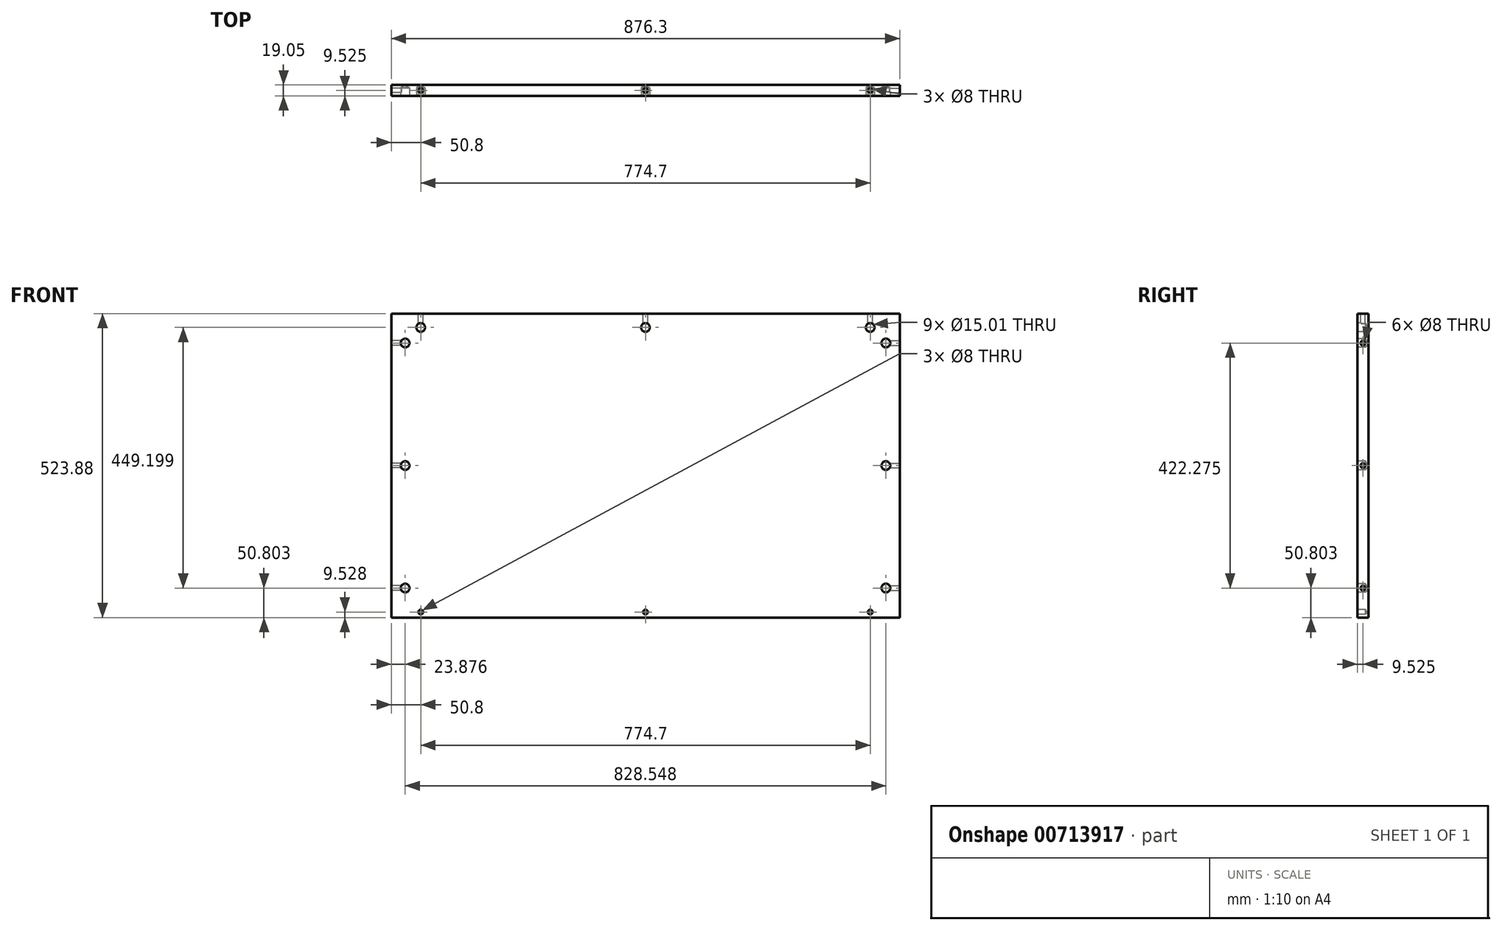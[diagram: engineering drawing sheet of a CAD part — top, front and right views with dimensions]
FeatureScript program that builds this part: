
annotation { "Feature Type Name" : "Feature", "Feature Type Description" : "" }
export const myFeature = defineFeature(function(context is Context, id is Id, definition is map)
    precondition{}
    {
        {
            var Q0;
            Q0=qCreatedBy(makeId("Front.planeOp"),FACE);
            var sketch = newSketch(context, id + "F0", { "sketchPlane" : qUnion([Q0])});
            skLineSegment(sketch, "E0.bottom", {"start": v(438.15, 261.94) * mm, "end": v(-438.15, 261.94) * mm});
            skLineSegment(sketch, "E0.top", {"start": v(438.15, -261.94) * mm, "end": v(-438.15, -261.94) * mm});
            skLineSegment(sketch, "E0.left", {"start": v(438.15, 261.94) * mm, "end": v(438.15, -261.94) * mm});
            skLineSegment(sketch, "E0.right", {"start": v(-438.15, 261.94) * mm, "end": v(-438.15, -261.94) * mm});
            skPoint(sketch, "E0.middle", {"position": v(0, 0) * mm});
            skSolve(sketch);
        }
        {
            var Q0;
            Q0=makeQuery(id+"F0.imprint","IMPRINT",FACE,{"disambiguationData":[TD([[makeQuery(id+"F0.imprint","IMPRINT",EDGE,{"derivedFrom":sQuery(id+"F0.wireOp",EDGE,"E0.bottom")}),1.0]])]});
            extrude(context, id + "F1", {"entities" : qUnion([Q0]), "depth" : 19.05 * mm, "offsetDistance" : 25.4 * mm});
        }
        {
            var Q0;
            Q0=makeQuery(id+"F1.opExtrude","CAP_FACE",FACE,{"disambiguationData":[OSD([sQuery(id+"F0.wireOp",EDGE,"E0.bottom"),sQuery(id+"F0.wireOp",EDGE,"E0.top"),sQuery(id+"F0.wireOp",EDGE,"E0.left"),sQuery(id+"F0.wireOp",EDGE,"E0.right")])],"isStart":false});
            var sketch = newSketch(context, id + "F2", { "sketchPlane" : qUnion([Q0])});
            skLineSegment(sketch, "E1", {"start": v(-438.15, 261.94) * mm, "end": v(-414.27, 261.94) * mm});
            skLineSegment(sketch, "E2", {"start": v(-414.27, 261.94) * mm, "end": v(-414.27, -261.94) * mm});
            skLineSegment(sketch, "E3", {"start": v(438.15, 261.94) * mm, "end": v(414.27, 261.94) * mm});
            skLineSegment(sketch, "E4", {"start": v(414.27, 261.94) * mm, "end": v(414.27, -261.94) * mm});
            skLineSegment(sketch, "E5", {"start": v(-438.15, -261.94) * mm, "end": v(-438.15, -252.41) * mm});
            skLineSegment(sketch, "E6", {"start": v(-438.15, -252.41) * mm, "end": v(438.15, -252.41) * mm});
            skLineSegment(sketch, "E7", {"start": v(-438.15, 261.94) * mm, "end": v(-438.15, 238.06) * mm});
            skLineSegment(sketch, "E8", {"start": v(-438.15, 238.06) * mm, "end": v(438.15, 238.06) * mm});
            skLineSegment(sketch, "E9", {"start": v(0, 238.06) * mm, "end": v(0, 261.94) * mm});
            skLineSegment(sketch, "E10", {"start": v(-414.27, 0) * mm, "end": v(-438.15, 0) * mm});
            skLineSegment(sketch, "E11", {"start": v(414.27, 0) * mm, "end": v(438.15, 0) * mm});
            skLineSegment(sketch, "E12", {"start": v(0, -261.94) * mm, "end": v(0, -252.41) * mm});
            skLineSegment(sketch, "E13", {"start": v(-438.15, -252.41) * mm, "end": v(-387.35, -252.41) * mm});
            skLineSegment(sketch, "E14", {"start": v(438.15, -252.41) * mm, "end": v(387.35, -252.41) * mm});
            skLineSegment(sketch, "E15", {"start": v(-414.27, 261.94) * mm, "end": v(-414.27, 211.14) * mm});
            skLineSegment(sketch, "E16", {"start": v(-414.27, -261.94) * mm, "end": v(-414.27, -211.14) * mm});
            skLineSegment(sketch, "E17", {"start": v(414.27, -261.94) * mm, "end": v(414.27, -211.14) * mm});
            skLineSegment(sketch, "E18", {"start": v(414.27, 261.94) * mm, "end": v(414.27, 211.14) * mm});
            skLineSegment(sketch, "E19", {"start": v(-438.15, 238.06) * mm, "end": v(-387.35, 238.06) * mm});
            skLineSegment(sketch, "E20", {"start": v(438.15, 238.06) * mm, "end": v(387.35, 238.06) * mm});
            skPoint(sketch, "E21", {"position": v(-387.35, 238.06) * mm});
            skPoint(sketch, "E22", {"position": v(-414.27, 211.14) * mm});
            skPoint(sketch, "E23", {"position": v(0, 238.06) * mm});
            skPoint(sketch, "E24", {"position": v(387.35, 238.06) * mm});
            skPoint(sketch, "E25", {"position": v(414.27, 211.14) * mm});
            skPoint(sketch, "E26", {"position": v(414.27, 0) * mm});
            skPoint(sketch, "E27", {"position": v(-414.27, 0) * mm});
            skPoint(sketch, "E28", {"position": v(414.27, -211.14) * mm});
            skPoint(sketch, "E29", {"position": v(387.35, -252.41) * mm});
            skPoint(sketch, "E30", {"position": v(0, -252.41) * mm});
            skPoint(sketch, "E31", {"position": v(-387.35, -252.41) * mm});
            skPoint(sketch, "E32", {"position": v(-414.27, -211.14) * mm});
            skSolve(sketch);
        }
        {
            var Q0;
            Q0=sQuery(id+"F2.wireOp",VERTEX,"E21");
            var Q1;
            Q1=sQuery(id+"F2.wireOp",VERTEX,"E22");
            var Q2;
            Q2=sQuery(id+"F2.wireOp",VERTEX,"E27");
            var Q3;
            Q3=sQuery(id+"F2.wireOp",VERTEX,"E32");
            var Q4;
            Q4=sQuery(id+"F2.wireOp",VERTEX,"E23");
            var Q5;
            Q5=sQuery(id+"F2.wireOp",VERTEX,"E24");
            var Q6;
            Q6=sQuery(id+"F2.wireOp",VERTEX,"E25");
            var Q7;
            Q7=sQuery(id+"F2.wireOp",VERTEX,"E26");
            var Q8;
            Q8=sQuery(id+"F2.wireOp",VERTEX,"E28");
            var Q9;
            Q9=makeQuery(id+"F1.opExtrude","SWEPT_BODY",BODY,{"disambiguationData":[OSD([sQuery(id+"F0.wireOp",EDGE,"E0.bottom"),sQuery(id+"F0.wireOp",EDGE,"E0.top"),sQuery(id+"F0.wireOp",EDGE,"E0.left"),sQuery(id+"F0.wireOp",EDGE,"E0.right")])]});
            hole(context, id + "F3", {"style" : HoleStyle.SIMPLE, "endStyle" : HoleEndStyle.BLIND, "holeDiameter" : 15 * mm, "majorDiameter" : 6.35 * mm, "holeDepth" : 14.22 * mm, "isTappedThrough" : true, "tappedDepth" : 12.7 * mm, "tapClearance" : 3, "startFromSketch" : true, "locations" : qUnion([Q0, Q1, Q2, Q3, Q4, Q5, Q6, Q7, Q8]), "scope" : qUnion([Q9])});
        }
        {
            var Q0;
            Q0=sQuery(id+"F2.wireOp",VERTEX,"E31");
            var Q1;
            Q1=sQuery(id+"F2.wireOp",VERTEX,"E30");
            var Q2;
            Q2=sQuery(id+"F2.wireOp",VERTEX,"E29");
            var Q3;
            Q3=makeQuery(id+"F1.opExtrude","SWEPT_BODY",BODY,{"disambiguationData":[OSD([sQuery(id+"F0.wireOp",EDGE,"E0.bottom"),sQuery(id+"F0.wireOp",EDGE,"E0.top"),sQuery(id+"F0.wireOp",EDGE,"E0.left"),sQuery(id+"F0.wireOp",EDGE,"E0.right")])]});
            hole(context, id + "F4", {"style" : HoleStyle.SIMPLE, "endStyle" : HoleEndStyle.BLIND, "holeDiameter" : 8 * mm, "majorDiameter" : 6.35 * mm, "holeDepth" : 14.22 * mm, "isTappedThrough" : true, "tappedDepth" : 12.7 * mm, "tapClearance" : 3, "startFromSketch" : true, "locations" : qUnion([Q0, Q1, Q2]), "scope" : qUnion([Q3])});
        }
        {
            var Q0;
            Q0=makeQuery(id+"F1.opExtrude","SWEPT_FACE",FACE,{"disambiguationData":[OSD([sQuery(id+"F0.wireOp",EDGE,"E0.left")])]});
            var sketch = newSketch(context, id + "F5", { "sketchPlane" : qUnion([Q0])});
            skLineSegment(sketch, "E33", {"start": v(-9.53, 261.94) * mm, "end": v(-9.53, 211.14) * mm});
            skLineSegment(sketch, "E34", {"start": v(-9.53, -261.94) * mm, "end": v(-9.53, -211.14) * mm});
            skLineSegment(sketch, "E35", {"start": v(-19.05, 0) * mm, "end": v(-9.53, 0) * mm});
            skPoint(sketch, "E36", {"position": v(-9.53, 211.14) * mm});
            skPoint(sketch, "E37", {"position": v(-9.53, 0) * mm});
            skPoint(sketch, "E38", {"position": v(-9.53, -211.14) * mm});
            skSolve(sketch);
        }
        {
            var Q0;
            Q0=sQuery(id+"F5.wireOp",VERTEX,"E36");
            var Q1;
            Q1=sQuery(id+"F5.wireOp",VERTEX,"E37");
            var Q2;
            Q2=sQuery(id+"F5.wireOp",VERTEX,"E38");
            var Q3;
            Q3=makeQuery(id+"F1.opExtrude","SWEPT_BODY",BODY,{"disambiguationData":[OSD([sQuery(id+"F0.wireOp",EDGE,"E0.bottom"),sQuery(id+"F0.wireOp",EDGE,"E0.top"),sQuery(id+"F0.wireOp",EDGE,"E0.left"),sQuery(id+"F0.wireOp",EDGE,"E0.right")])]});
            hole(context, id + "F6", {"style" : HoleStyle.SIMPLE, "endStyle" : HoleEndStyle.BLIND, "holeDiameter" : 8 * mm, "majorDiameter" : 6.35 * mm, "holeDepth" : 25.4 * mm, "isTappedThrough" : true, "tappedDepth" : 12.7 * mm, "tapClearance" : 3, "startFromSketch" : true, "locations" : qUnion([Q0, Q1, Q2]), "scope" : qUnion([Q3])});
        }
        {
            var Q0;
            Q0=makeQuery(id+"F1.opExtrude","SWEPT_FACE",FACE,{"disambiguationData":[OSD([sQuery(id+"F0.wireOp",EDGE,"E0.right")])]});
            var sketch = newSketch(context, id + "F7", { "sketchPlane" : qUnion([Q0])});
            skLineSegment(sketch, "E39", {"start": v(9.53, 261.94) * mm, "end": v(9.53, 211.14) * mm});
            skLineSegment(sketch, "E40", {"start": v(19.05, 0) * mm, "end": v(9.53, 0) * mm});
            skLineSegment(sketch, "E41", {"start": v(9.53, -261.94) * mm, "end": v(9.53, -211.14) * mm});
            skSolve(sketch);
        }
        {
            var Q0;
            Q0=sQuery(id+"F7.wireOp",VERTEX,"E39.end");
            var Q1;
            Q1=sQuery(id+"F7.wireOp",VERTEX,"E40.end");
            var Q2;
            Q2=sQuery(id+"F7.wireOp",VERTEX,"E41.end");
            var Q3;
            Q3=makeQuery(id+"F1.opExtrude","SWEPT_BODY",BODY,{"disambiguationData":[OSD([sQuery(id+"F0.wireOp",EDGE,"E0.bottom"),sQuery(id+"F0.wireOp",EDGE,"E0.top"),sQuery(id+"F0.wireOp",EDGE,"E0.left"),sQuery(id+"F0.wireOp",EDGE,"E0.right")])]});
            hole(context, id + "F8", {"style" : HoleStyle.SIMPLE, "endStyle" : HoleEndStyle.BLIND, "holeDiameter" : 8 * mm, "majorDiameter" : 6.35 * mm, "holeDepth" : 25.4 * mm, "isTappedThrough" : true, "tappedDepth" : 12.7 * mm, "tapClearance" : 3, "startFromSketch" : true, "locations" : qUnion([Q0, Q1, Q2]), "scope" : qUnion([Q3])});
        }
        {
            var Q0;
            Q0=makeQuery(id+"F1.opExtrude","SWEPT_FACE",FACE,{"disambiguationData":[OSD([sQuery(id+"F0.wireOp",EDGE,"E0.bottom")])]});
            var sketch = newSketch(context, id + "F9", { "sketchPlane" : qUnion([Q0])});
            skLineSegment(sketch, "E42", {"start": v(-438.15, -9.53) * mm, "end": v(-387.35, -9.53) * mm});
            skLineSegment(sketch, "E43", {"start": v(0, -19.05) * mm, "end": v(0, -9.53) * mm});
            skLineSegment(sketch, "E44", {"start": v(438.15, -9.53) * mm, "end": v(387.35, -9.53) * mm});
            skPoint(sketch, "E45", {"position": v(-387.35, -9.53) * mm});
            skPoint(sketch, "E46", {"position": v(0, -9.53) * mm});
            skPoint(sketch, "E47", {"position": v(387.35, -9.53) * mm});
            skSolve(sketch);
        }
        {
            var Q0;
            Q0=sQuery(id+"F9.wireOp",VERTEX,"E45");
            var Q1;
            Q1=sQuery(id+"F9.wireOp",VERTEX,"E46");
            var Q2;
            Q2=sQuery(id+"F9.wireOp",VERTEX,"E47");
            var Q3;
            Q3=makeQuery(id+"F1.opExtrude","SWEPT_BODY",BODY,{"disambiguationData":[OSD([sQuery(id+"F0.wireOp",EDGE,"E0.bottom"),sQuery(id+"F0.wireOp",EDGE,"E0.top"),sQuery(id+"F0.wireOp",EDGE,"E0.left"),sQuery(id+"F0.wireOp",EDGE,"E0.right")])]});
            hole(context, id + "F10", {"style" : HoleStyle.SIMPLE, "endStyle" : HoleEndStyle.BLIND, "holeDiameter" : 8 * mm, "majorDiameter" : 6.35 * mm, "holeDepth" : 25.4 * mm, "isTappedThrough" : true, "tappedDepth" : 12.7 * mm, "tapClearance" : 3, "startFromSketch" : true, "locations" : qUnion([Q0, Q1, Q2]), "scope" : qUnion([Q3])});
        }
    });
